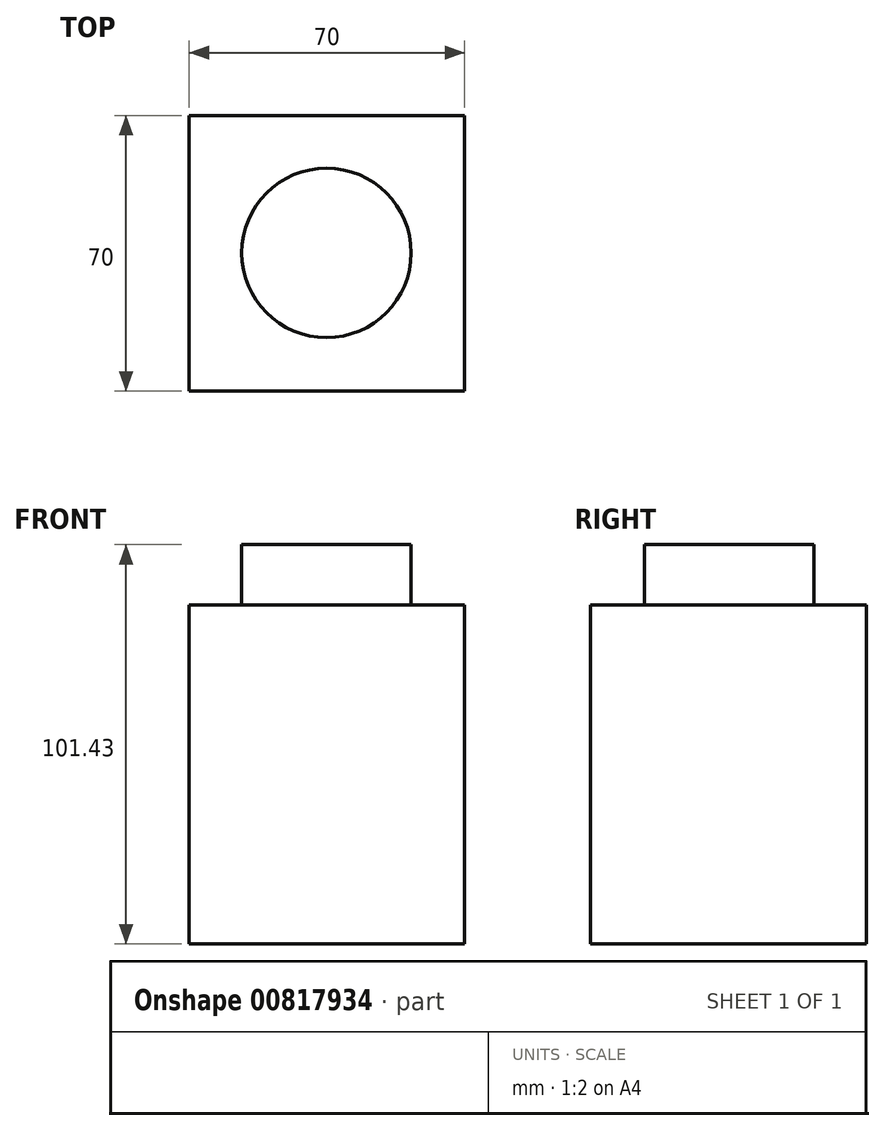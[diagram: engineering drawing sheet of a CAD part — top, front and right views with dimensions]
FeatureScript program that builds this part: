
annotation { "Feature Type Name" : "Feature", "Feature Type Description" : "" }
export const myFeature = defineFeature(function(context is Context, id is Id, definition is map)
    precondition{}
    {
        {
            assignVariable(context, id + "F0", {"name" : "Square", "anyValue" : 70});
        }
        {
            assignVariable(context, id + "F1", {"name" : "Height", "anyValue" : 1.23 * getVariable(context, 'Square')});
        }
        {
            assignVariable(context, id + "F2", {"name" : "Step", "anyValue" : .218 * getVariable(context, 'Square')});
        }
        {
            var Q0;
            Q0=qCreatedBy(makeId("Top.planeOp"),FACE);
            var sketch = newSketch(context, id + "F3", { "sketchPlane" : qUnion([Q0])});
            skLineSegment(sketch, "E0.bottom", {"start": v(35, 35) * mm, "end": v(-35, 35) * mm});
            skLineSegment(sketch, "E0.top", {"start": v(35, -35) * mm, "end": v(-35, -35) * mm});
            skLineSegment(sketch, "E0.left", {"start": v(35, 35) * mm, "end": v(35, -35) * mm});
            skLineSegment(sketch, "E0.right", {"start": v(-35, 35) * mm, "end": v(-35, -35) * mm});
            skPoint(sketch, "E0.middle", {"position": v(0, 0) * mm});
            skSolve(sketch);
        }
        {
            var Q0;
            Q0=qSketchRegion(id+"F3",true);
            extrude(context, id + "F4", {"entities" : qUnion([Q0]), "depth" : (getVariable(context, 'Height')) * mm, "offsetDistance" : 25 * mm});
        }
        {
            var Q0;
            Q0=makeQuery(id+"F4.opExtrude","CAP_FACE",FACE,{"disambiguationData":[OSD([sQuery(id+"F3.wireOp",EDGE,"E0.bottom"),sQuery(id+"F3.wireOp",EDGE,"E0.top"),sQuery(id+"F3.wireOp",EDGE,"E0.left"),sQuery(id+"F3.wireOp",EDGE,"E0.right")])],"isStart":false});
            var sketch = newSketch(context, id + "F5", { "sketchPlane" : qUnion([Q0])});
            skCircle(sketch, "E1", {"center": v(-0.13, 0.13) * mm, "radius": 21.53 * mm});
            skSolve(sketch);
        }
        {
            var Q0;
            Q0=makeQuery(id+"F5.imprint","IMPRINT",FACE,{"disambiguationData":[TD([[makeQuery(id+"F5.imprint","IMPRINT",EDGE,{"derivedFrom":sQuery(id+"F5.wireOp",EDGE,"E1")}),1.0]])]});
            extrude(context, id + "F6", {"entities" : qUnion([Q0]), "operationType" : NewBodyOperationType.ADD, "depth" : (getVariable(context, 'Step')) * mm, "offsetDistance" : 25 * mm});
        }
    });
